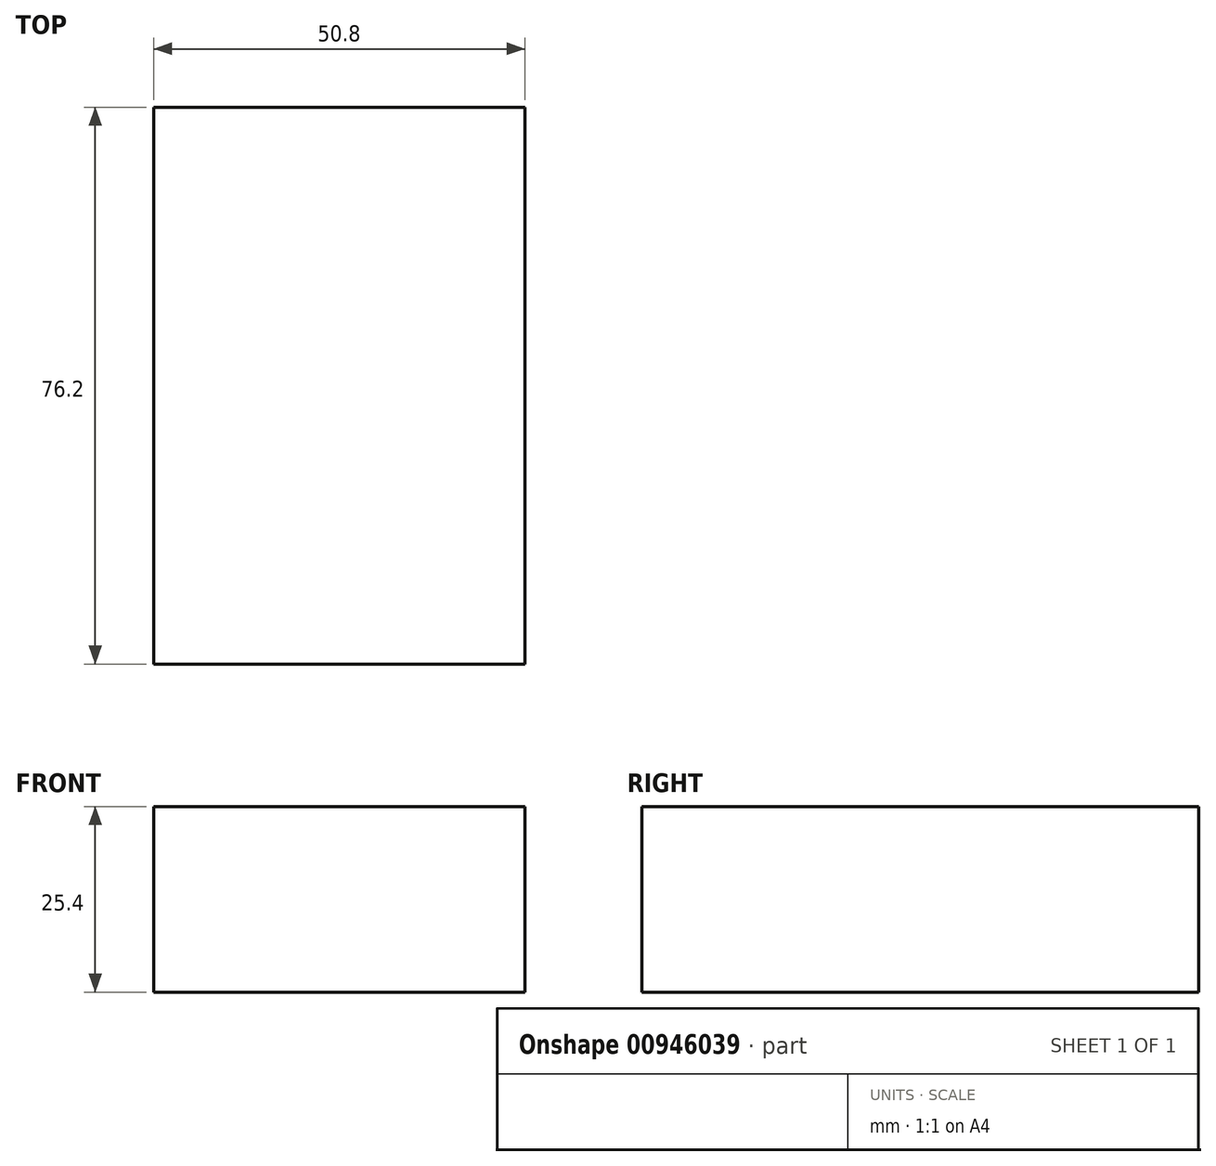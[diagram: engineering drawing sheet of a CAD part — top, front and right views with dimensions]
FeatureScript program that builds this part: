
annotation { "Feature Type Name" : "Feature", "Feature Type Description" : "" }
export const myFeature = defineFeature(function(context is Context, id is Id, definition is map)
    precondition{}
    {
        {
            var Q0;
            Q0=qCreatedBy(makeId("Top.planeOp"),FACE);
            var sketch = newSketch(context, id + "F0", { "sketchPlane" : qUnion([Q0])});
            skLineSegment(sketch, "E0.bottom", {"start": v(-25.4, 38.1) * mm, "end": v(25.4, 38.1) * mm});
            skLineSegment(sketch, "E0.top", {"start": v(-25.4, -38.1) * mm, "end": v(25.4, -38.1) * mm});
            skLineSegment(sketch, "E0.left", {"start": v(-25.4, 38.1) * mm, "end": v(-25.4, -38.1) * mm});
            skLineSegment(sketch, "E0.right", {"start": v(25.4, 38.1) * mm, "end": v(25.4, -38.1) * mm});
            skSolve(sketch);
        }
        {
            var Q0;
            Q0=makeQuery(id+"F0.imprint","IMPRINT",FACE,{"disambiguationData":[TD([[makeQuery(id+"F0.imprint","IMPRINT",EDGE,{"derivedFrom":sQuery(id+"F0.wireOp",EDGE,"E0.bottom")}),-1.0]])]});
            extrude(context, id + "F1", {"entities" : qUnion([Q0]), "depth" : 25.4 * mm, "offsetDistance" : 25.4 * mm});
        }
    });
